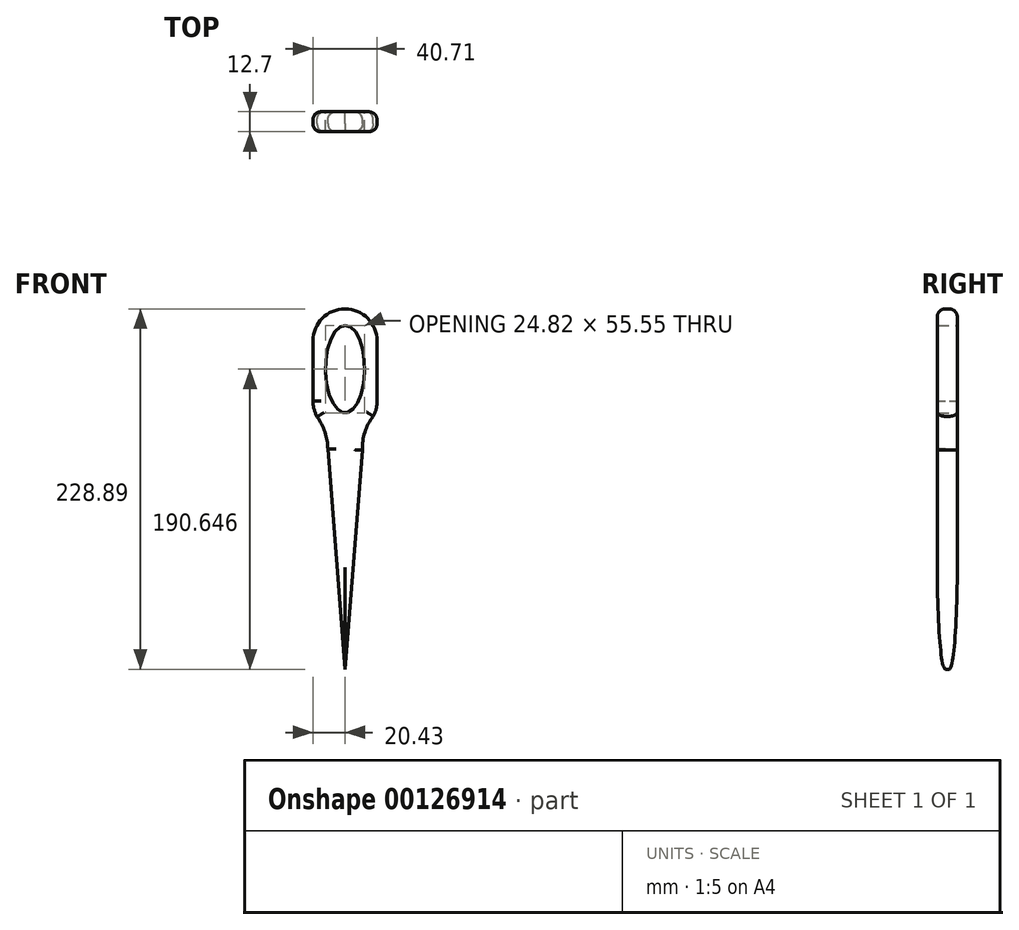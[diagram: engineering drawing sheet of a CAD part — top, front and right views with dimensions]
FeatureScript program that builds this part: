
annotation { "Feature Type Name" : "Feature", "Feature Type Description" : "" }
export const myFeature = defineFeature(function(context is Context, id is Id, definition is map)
    precondition{}
    {
        {
            var Q0;
            Q0=qCreatedBy(makeId("Front.planeOp"),FACE);
            var sketch = newSketch(context, id + "F0", { "sketchPlane" : qUnion([Q0])});
            skArc(sketch, "E0", {"start": v(20.24, 38.14) * mm, "mid": v(-0.1, 58.46) * mm, "end": v(-20.43, 38.14) * mm});
            skLineSegment(sketch, "E1", {"start": v(-20.43, 38.14) * mm, "end": v(-20.43, 0) * mm});
            skLineSegment(sketch, "E2", {"start": v(20.24, 38.14) * mm, "end": v(20.28, 0) * mm});
            skArc(sketch, "E3", {"start": v(-20.43, 0) * mm, "mid": v(-0.08, -20.38) * mm, "end": v(20.28, 0) * mm});
            skArc(sketch, "E4", {"start": v(-10.98, -30.67) * mm, "mid": v(-12.84, -19.88) * mm, "end": v(-17.77, -10.1) * mm});
            skArc(sketch, "E5", {"start": v(17.8, -9.77) * mm, "mid": v(12.5, -19.84) * mm, "end": v(11, -31.1) * mm});
            skEllipse(sketch, "E6", {"center": v(0, 20.22) * mm, "majorRadius": 27.78 * mm, "minorRadius": 12.4 * mm, "majorAxis": v(0, 1)});
            skLineSegment(sketch, "E7", {"start": v(-10.98, -30.67) * mm, "end": v(0, -170.43) * mm});
            skLineSegment(sketch, "E8", {"start": v(0, -170.43) * mm, "end": v(11, -31.1) * mm});
            skSolve(sketch);
        }
        {
            var Q0;
            Q0=makeQuery(id+"F0.imprint","IMPRINT",FACE,{"disambiguationData":[TD([[makeQuery(id+"F0.imprint","IMPRINT",EDGE,{"derivedFrom":sQuery(id+"F0.wireOp",EDGE,"E0")}),1.0]])]});
            var Q1;
            {var subQ0=sQuery(id+"F0.wireOp",EDGE,"HrbUxuRM-qgPz-BCtL-NFr4-QfKUrBvUR983");Q1=makeQuery(id+"F0.imprint","IMPRINT",FACE,{"disambiguationData":[TD([[makeQuery(id+"F0.imprint","IMPRINT",EDGE,{"derivedFrom":subQ0}),1.0]])]});}
            var Q2;
            {var subQ0=sQuery(id+"F0.wireOp",EDGE,"E7");Q2=makeQuery(id+"F0.imprint","IMPRINT",FACE,{"disambiguationData":[TD([[makeQuery(id+"F0.imprint","IMPRINT",EDGE,{"derivedFrom":subQ0}),1.0]])]});}
            extrude(context, id + "F1", {"entities" : qUnion([Q0, Q1, Q2]), "depth" : 12.7 * mm});
        }
        {
            var Q0;
            Q0=makeQuery(id+"F1.opExtrude","CAP_EDGE",EDGE,{"disambiguationData":[OSD([sQuery(id+"F0.wireOp",EDGE,"E0")])],"isStart":false});
            var Q1;
            Q1=makeQuery(id+"F1.opExtrude","CAP_EDGE",EDGE,{"disambiguationData":[OSD([sQuery(id+"F0.wireOp",EDGE,"E0")])],"isStart":true});
            var Q2;
            Q2=makeQuery(id+"F1.opExtrude","CAP_EDGE",EDGE,{"disambiguationData":[OSD([sQuery(id+"F0.wireOp",EDGE,"E1")])],"isStart":false});
            var Q3;
            Q3=makeQuery(id+"F1.opExtrude","CAP_EDGE",EDGE,{"disambiguationData":[OSD([sQuery(id+"F0.wireOp",EDGE,"E1")])],"isStart":true});
            var Q4;
            {var subQ0=sQuery(id+"F0.wireOp",EDGE,"E3");Q4=makeQuery(id+"F1.opExtrude","CAP_EDGE",EDGE,{"disambiguationData":[OSD([subQ0]),TDD([makeQuery(id+"F0.imprint","IMPRINT",EDGE,{"disambiguationData":[TD([[makeQuery(id+"F0.imprint","INTERSECT",VERTEX,{"derivedFrom":[sQuery(id+"F0.wireOp",EDGE,"E1"),subQ0]}),-1.0]])],"derivedFrom":subQ0})])],"isStart":false});}
            var Q5;
            {var subQ0=sQuery(id+"F0.wireOp",EDGE,"E3");Q5=makeQuery(id+"F1.opExtrude","CAP_EDGE",EDGE,{"disambiguationData":[OSD([subQ0]),TDD([makeQuery(id+"F0.imprint","IMPRINT",EDGE,{"disambiguationData":[TD([[makeQuery(id+"F0.imprint","INTERSECT",VERTEX,{"derivedFrom":[sQuery(id+"F0.wireOp",EDGE,"E1"),subQ0]}),-1.0]])],"derivedFrom":subQ0})])],"isStart":true});}
            var Q6;
            Q6=makeQuery(id+"F1.opExtrude","CAP_EDGE",EDGE,{"disambiguationData":[OSD([sQuery(id+"F0.wireOp",EDGE,"E4")])],"isStart":false});
            var Q7;
            Q7=makeQuery(id+"F1.opExtrude","CAP_EDGE",EDGE,{"disambiguationData":[OSD([sQuery(id+"F0.wireOp",EDGE,"E4")])],"isStart":true});
            var Q8;
            Q8=makeQuery(id+"F1.opExtrude","CAP_EDGE",EDGE,{"disambiguationData":[OSD([sQuery(id+"F0.wireOp",EDGE,"HrbUxuRM-qgPz-BCtL-NFr4-QfKUrBvUR983")])],"isStart":false});
            var Q9;
            Q9=makeQuery(id+"F1.opExtrude","CAP_EDGE",EDGE,{"disambiguationData":[OSD([sQuery(id+"F0.wireOp",EDGE,"HrbUxuRM-qgPz-BCtL-NFr4-QfKUrBvUR983")])],"isStart":true});
            var Q10;
            {var subQ0=sQuery(id+"F0.wireOp",EDGE,"E3");Q10=makeQuery(id+"F1.opExtrude","CAP_EDGE",EDGE,{"disambiguationData":[OSD([subQ0]),TDD([makeQuery(id+"F0.imprint","IMPRINT",EDGE,{"disambiguationData":[TD([[makeQuery(id+"F0.imprint","INTERSECT",VERTEX,{"derivedFrom":[sQuery(id+"F0.wireOp",EDGE,"E2"),subQ0]}),1.0]])],"derivedFrom":subQ0})])],"isStart":false});}
            var Q11;
            {var subQ0=sQuery(id+"F0.wireOp",EDGE,"E3");Q11=makeQuery(id+"F1.opExtrude","CAP_EDGE",EDGE,{"disambiguationData":[OSD([subQ0]),TDD([makeQuery(id+"F0.imprint","IMPRINT",EDGE,{"disambiguationData":[TD([[makeQuery(id+"F0.imprint","INTERSECT",VERTEX,{"derivedFrom":[sQuery(id+"F0.wireOp",EDGE,"E2"),subQ0]}),1.0]])],"derivedFrom":subQ0})])],"isStart":true});}
            var Q12;
            Q12=makeQuery(id+"F1.opExtrude","CAP_EDGE",EDGE,{"disambiguationData":[OSD([sQuery(id+"F0.wireOp",EDGE,"E5")])],"isStart":false});
            var Q13;
            Q13=makeQuery(id+"F1.opExtrude","CAP_EDGE",EDGE,{"disambiguationData":[OSD([sQuery(id+"F0.wireOp",EDGE,"E5")])],"isStart":true});
            var Q14;
            Q14=makeQuery(id+"F1.opExtrude","CAP_EDGE",EDGE,{"disambiguationData":[OSD([sQuery(id+"F0.wireOp",EDGE,"h0EXn7xT-qhaa-N3Vm-RoHN-ix8iVNZh4NX5")])],"isStart":false});
            var Q15;
            Q15=makeQuery(id+"F1.opExtrude","CAP_EDGE",EDGE,{"disambiguationData":[OSD([sQuery(id+"F0.wireOp",EDGE,"h0EXn7xT-qhaa-N3Vm-RoHN-ix8iVNZh4NX5")])],"isStart":true});
            var Q16;
            Q16=makeQuery(id+"F1.opExtrude","CAP_EDGE",EDGE,{"disambiguationData":[OSD([sQuery(id+"F0.wireOp",EDGE,"E7")])],"isStart":false});
            var Q17;
            Q17=makeQuery(id+"F1.opExtrude","CAP_EDGE",EDGE,{"disambiguationData":[OSD([sQuery(id+"F0.wireOp",EDGE,"E7")])],"isStart":true});
            var Q18;
            Q18=makeQuery(id+"F1.opExtrude","CAP_EDGE",EDGE,{"disambiguationData":[OSD([sQuery(id+"F0.wireOp",EDGE,"E8")])],"isStart":false});
            var Q19;
            Q19=makeQuery(id+"F1.opExtrude","CAP_EDGE",EDGE,{"disambiguationData":[OSD([sQuery(id+"F0.wireOp",EDGE,"E8")])],"isStart":true});
            fillet(context, id + "F2", {"entities" : qUnion([Q0, Q1, Q2, Q3, Q4, Q5, Q6, Q7, Q8, Q9, Q10, Q11, Q12, Q13, Q14, Q15, Q16, Q17, Q18, Q19]), "radius" : 5.08 * mm, "tangentPropagation" : true, "allowEdgeOverflow" : false});
        }
    });
